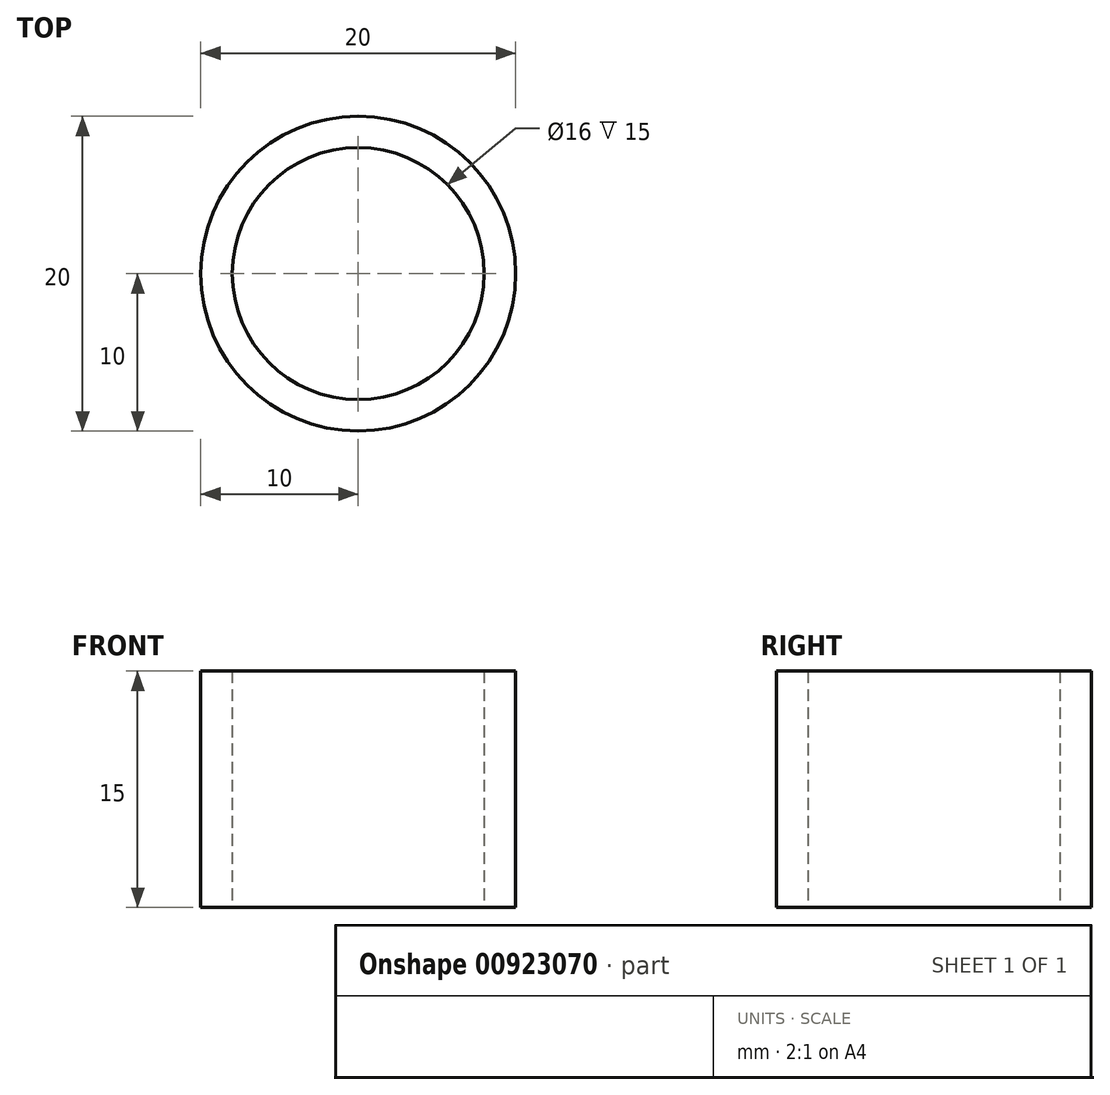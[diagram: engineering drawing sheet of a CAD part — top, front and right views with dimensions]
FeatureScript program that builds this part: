
annotation { "Feature Type Name" : "Feature", "Feature Type Description" : "" }
export const myFeature = defineFeature(function(context is Context, id is Id, definition is map)
    precondition{}
    {
        {
            var Q0;
            Q0=qCreatedBy(makeId("Top.planeOp"),FACE);
            var sketch = newSketch(context, id + "F0", { "sketchPlane" : qUnion([Q0])});
            skCircle(sketch, "E0", {"center": v(0, 0) * mm, "radius": 10 * mm});
            skCircle(sketch, "E1", {"center": v(0, 0) * mm, "radius": 8 * mm});
            skSolve(sketch);
        }
        {
            var Q0;
            Q0=makeQuery(id+"F0.imprint","IMPRINT",FACE,{"disambiguationData":[TD([[makeQuery(id+"F0.imprint","IMPRINT",EDGE,{"derivedFrom":sQuery(id+"F0.wireOp",EDGE,"E0")}),1.0]])]});
            extrude(context, id + "F1", {"entities" : qUnion([Q0]), "depth" : 15 * mm, "offsetDistance" : 25 * mm});
        }
    });
